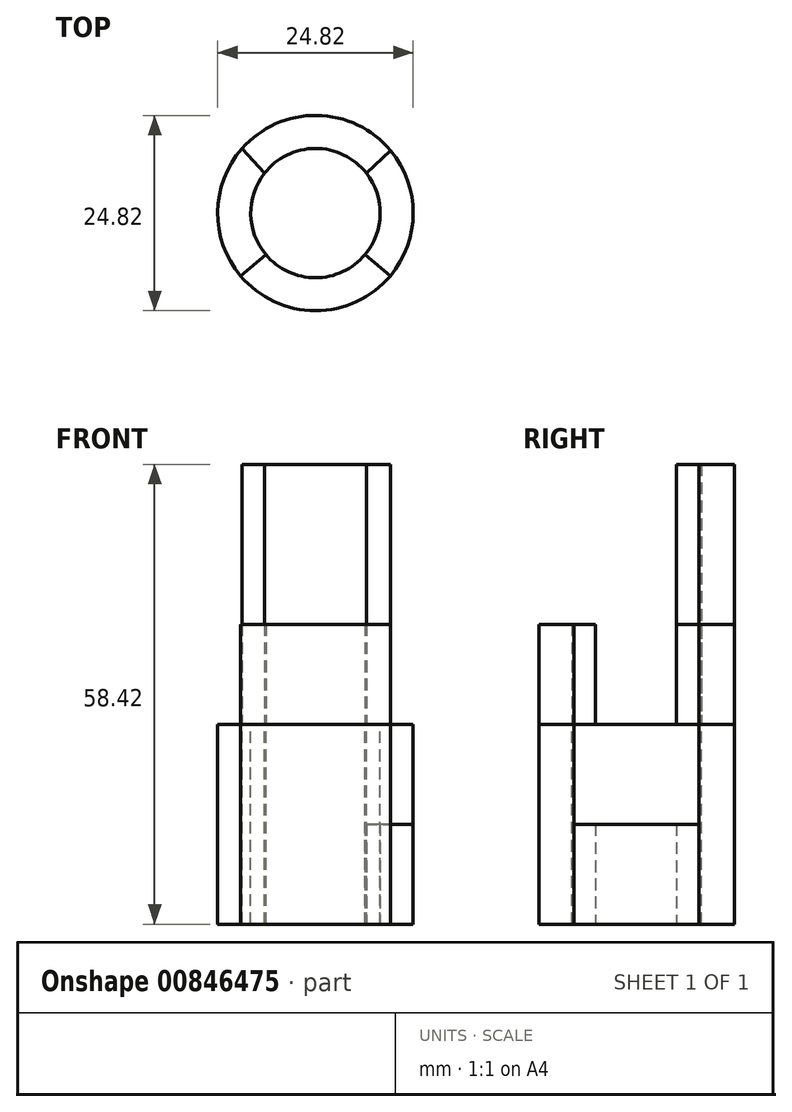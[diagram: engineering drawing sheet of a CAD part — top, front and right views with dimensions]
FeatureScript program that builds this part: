
annotation { "Feature Type Name" : "Feature", "Feature Type Description" : "" }
export const myFeature = defineFeature(function(context is Context, id is Id, definition is map)
    precondition{}
    {
        {
            var Q0;
            Q0=qCreatedBy(makeId("Top.planeOp"),FACE);
            var sketch = newSketch(context, id + "F0", { "sketchPlane" : qUnion([Q0])});
            skCircle(sketch, "E0", {"center": v(0, 0) * mm, "radius": 12.41 * mm});
            skCircle(sketch, "E1", {"center": v(0, 0) * mm, "radius": 8.21 * mm});
            skLineSegment(sketch, "E2", {"start": v(0, 0) * mm, "end": v(-9.5, -7.98) * mm});
            skLineSegment(sketch, "E3", {"start": v(0, 0) * mm, "end": v(9.5, -7.98) * mm});
            skArc(sketch, "E4", {"start": v(9.56, 7.92) * mm, "mid": v(0.17, 12.41) * mm, "end": v(-9.35, 8.17) * mm});
            skLineSegment(sketch, "E5", {"start": v(9.56, 7.92) * mm, "end": v(6.46, 5.07) * mm});
            skLineSegment(sketch, "E6", {"start": v(-9.35, 8.17) * mm, "end": v(-6.48, 5.05) * mm});
            skSolve(sketch);
        }
        {
            var Q0;
            {var subQ3=sQuery(id+"F0.wireOp",EDGE,"E6");Q0=makeQuery(id+"F0.imprint","IMPRINT",FACE,{"disambiguationData":[TD([[makeQuery(id+"F0.imprint","IMPRINT",EDGE,{"derivedFrom":subQ3}),-1.0]])]});}
            var Q1;
            {var subQ3=sQuery(id+"F0.wireOp",EDGE,"E5");Q1=makeQuery(id+"F0.imprint","IMPRINT",FACE,{"disambiguationData":[TD([[makeQuery(id+"F0.imprint","IMPRINT",EDGE,{"derivedFrom":subQ3}),1.0]])]});}
            extrude(context, id + "F1", {"entities" : qUnion([Q0, Q1]), "oppositeDirection" : true, "depth" : 25.4 * mm, "offsetDistance" : 25.4 * mm});
        }
        {
            var Q0;
            {var subQ0=sQuery(id+"F0.wireOp",EDGE,"E2");var subQ1=sQuery(id+"F0.wireOp",EDGE,"E0");var subQ2=makeQuery(id+"F0.imprint","INTERSECT",VERTEX,{"derivedFrom":[subQ1,subQ0]});Q0=makeQuery(id+"F0.imprint","IMPRINT",FACE,{"disambiguationData":[TD([[makeQuery(id+"F0.imprint","IMPRINT",EDGE,{"disambiguationData":[TD([[subQ2,-1.0]])],"derivedFrom":subQ1}),1.0]])]});}
            var Q1;
            Q1=makeQuery(id+"F1.opExtrude","CAP_FACE",FACE,{"disambiguationData":[OSD([sQuery(id+"F0.wireOp",EDGE,"E0"),sQuery(id+"F0.wireOp",EDGE,"E1"),sQuery(id+"F0.wireOp",EDGE,"E3"),sQuery(id+"F0.wireOp",EDGE,"E5")])],"isStart":false});
            var Q2;
            {var subQ0=sQuery(id+"F0.wireOp",EDGE,"E5");Q2=makeQuery(id+"F0.imprint","IMPRINT",FACE,{"disambiguationData":[TD([[makeQuery(id+"F0.imprint","IMPRINT",EDGE,{"derivedFrom":subQ0}),-1.0]])]});}
            extrude(context, id + "F2", {"entities" : qUnion([Q0, Q1, Q2]), "depth" : 12.7 * mm, "offsetDistance" : 25.4 * mm});
        }
        {
            var Q0;
            {var subQ0=sQuery(id+"F0.wireOp",EDGE,"E5");Q0=makeQuery(id+"F0.imprint","IMPRINT",FACE,{"disambiguationData":[TD([[makeQuery(id+"F0.imprint","IMPRINT",EDGE,{"derivedFrom":subQ0}),-1.0]])]});}
            extrude(context, id + "F3", {"entities" : qUnion([Q0]), "depth" : 33.02 * mm, "offsetDistance" : 25.4 * mm});
        }
        {
            var Q0;
            {var subQ0=sQuery(id+"F0.wireOp",EDGE,"E2");var subQ1=sQuery(id+"F0.wireOp",EDGE,"E0");var subQ2=makeQuery(id+"F0.imprint","INTERSECT",VERTEX,{"derivedFrom":[subQ1,subQ0]});Q0=makeQuery(id+"F0.imprint","IMPRINT",FACE,{"disambiguationData":[TD([[makeQuery(id+"F0.imprint","IMPRINT",EDGE,{"disambiguationData":[TD([[subQ2,-1.0]])],"derivedFrom":subQ1}),1.0]])]});}
            var Q1;
            {var subQ0=sQuery(id+"F0.wireOp",EDGE,"E5");Q1=makeQuery(id+"F0.imprint","IMPRINT",FACE,{"disambiguationData":[TD([[makeQuery(id+"F0.imprint","IMPRINT",EDGE,{"derivedFrom":subQ0}),-1.0]])]});}
            extrude(context, id + "F4", {"entities" : qUnion([Q0, Q1]), "oppositeDirection" : true, "depth" : 25.4 * mm, "offsetDistance" : 25.4 * mm});
        }
    });
